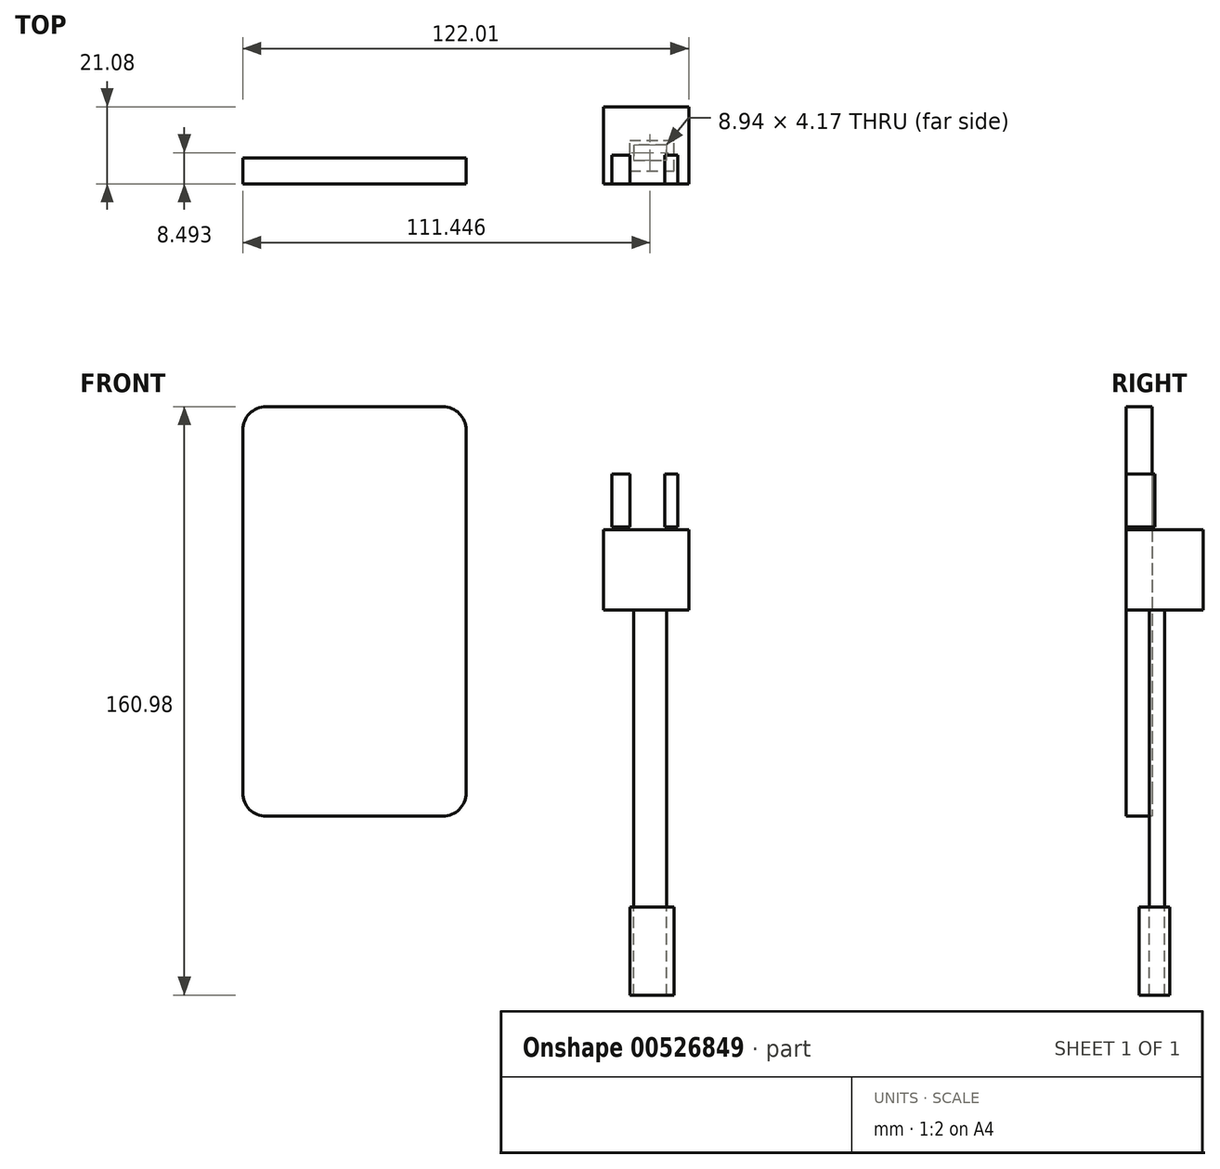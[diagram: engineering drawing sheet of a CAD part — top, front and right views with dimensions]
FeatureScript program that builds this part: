
annotation { "Feature Type Name" : "Feature", "Feature Type Description" : "" }
export const myFeature = defineFeature(function(context is Context, id is Id, definition is map)
    precondition{}
    {
        {
            var Q0;
            Q0=qCreatedBy(makeId("Front.planeOp"),FACE);
            var sketch = newSketch(context, id + "F0", { "sketchPlane" : qUnion([Q0])});
            skLineSegment(sketch, "E0", {"start": v(-53.04, 49.22) * mm, "end": v(-53.04, -50.12) * mm});
            skLineSegment(sketch, "E1", {"start": v(-46.7, 55.57) * mm, "end": v(1.7, 55.57) * mm});
            skLineSegment(sketch, "E2", {"start": v(8.05, 49.22) * mm, "end": v(8.05, -50.12) * mm});
            skLineSegment(sketch, "E3", {"start": v(-46.7, -56.47) * mm, "end": v(1.7, -56.47) * mm});
            skPoint(sketch, "E4.visualSharp", {"position": v(-53.04, 55.57) * mm});
            skArc(sketch, "E4.filletArc", {"start": v(-46.7, 55.57) * mm, "mid": v(-51.18, 53.72) * mm, "end": v(-53.04, 49.22) * mm});
            skPoint(sketch, "E5.visualSharp", {"position": v(8.05, 55.57) * mm});
            skArc(sketch, "E5.filletArc", {"start": v(8.05, 49.22) * mm, "mid": v(6.19, 53.72) * mm, "end": v(1.7, 55.57) * mm});
            skPoint(sketch, "E6.visualSharp", {"position": v(8.05, -56.47) * mm});
            skArc(sketch, "E6.filletArc", {"start": v(1.7, -56.47) * mm, "mid": v(6.19, -54.6) * mm, "end": v(8.05, -50.12) * mm});
            skPoint(sketch, "E7.visualSharp", {"position": v(-53.04, -56.47) * mm});
            skArc(sketch, "E7.filletArc", {"start": v(-53.04, -50.12) * mm, "mid": v(-51.18, -54.6) * mm, "end": v(-46.7, -56.47) * mm});
            skLineSegment(sketch, "E8", {"start": v(-43.71, 45.44) * mm, "end": v(-2.48, 45.44) * mm});
            skLineSegment(sketch, "E9", {"start": v(-50.06, 39.1) * mm, "end": v(-50.06, -39.99) * mm});
            skLineSegment(sketch, "E10", {"start": v(-43.71, -46.34) * mm, "end": v(-2.48, -46.34) * mm});
            skLineSegment(sketch, "E11", {"start": v(3.87, 39.1) * mm, "end": v(3.87, -39.99) * mm});
            skPoint(sketch, "E12.visualSharp", {"position": v(-50.06, 45.44) * mm});
            skArc(sketch, "E12.filletArc", {"start": v(-43.71, 45.44) * mm, "mid": v(-48.2, 43.58) * mm, "end": v(-50.06, 39.1) * mm});
            skPoint(sketch, "E13.visualSharp", {"position": v(3.87, 45.44) * mm});
            skArc(sketch, "E13.filletArc", {"start": v(3.87, 39.1) * mm, "mid": v(2.01, 43.58) * mm, "end": v(-2.48, 45.44) * mm});
            skPoint(sketch, "E14.visualSharp", {"position": v(3.87, -46.34) * mm});
            skArc(sketch, "E14.filletArc", {"start": v(-2.48, -46.34) * mm, "mid": v(2.01, -44.48) * mm, "end": v(3.87, -39.99) * mm});
            skPoint(sketch, "E15.visualSharp", {"position": v(-50.06, -46.34) * mm});
            skArc(sketch, "E15.filletArc", {"start": v(-50.06, -39.99) * mm, "mid": v(-48.2, -44.48) * mm, "end": v(-43.71, -46.34) * mm});
            skSolve(sketch);
        }
        {
            var Q0;
            Q0=makeQuery(id+"F0.imprint","IMPRINT",FACE,{"disambiguationData":[TD([[makeQuery(id+"F0.imprint","IMPRINT",EDGE,{"derivedFrom":sQuery(id+"F0.wireOp",EDGE,"E8")}),-1.0]])]});
            var Q1;
            Q1=makeQuery(id+"F0.imprint","IMPRINT",FACE,{"disambiguationData":[TD([[makeQuery(id+"F0.imprint","IMPRINT",EDGE,{"derivedFrom":sQuery(id+"F0.wireOp",EDGE,"E0")}),1.0]])]});
            extrude(context, id + "F1", {"entities" : qUnion([Q0, Q1]), "oppositeDirection" : true, "depth" : 7.11 * mm, "offsetDistance" : 25.4 * mm});
        }
        {
            var Q0;
            Q0=makeQuery(id+"F1.opExtrude","CAP_FACE",FACE,{"disambiguationData":[OSD([sQuery(id+"F0.wireOp",EDGE,"E0"),sQuery(id+"F0.wireOp",EDGE,"E1"),sQuery(id+"F0.wireOp",EDGE,"E2"),sQuery(id+"F0.wireOp",EDGE,"E3"),sQuery(id+"F0.wireOp",EDGE,"E4.filletArc"),sQuery(id+"F0.wireOp",EDGE,"E5.filletArc"),sQuery(id+"F0.wireOp",EDGE,"E6.filletArc"),sQuery(id+"F0.wireOp",EDGE,"E7.filletArc")])],"isStart":false});
            var sketch = newSketch(context, id + "F2", { "sketchPlane" : qUnion([Q0])});
            skLineSegment(sketch, "E16", {"start": v(-8.05, 44.55) * mm, "end": v(53.04, 44.55) * mm});
            skLineSegment(sketch, "E17", {"start": v(-8.05, -44.85) * mm, "end": v(53.04, -44.85) * mm});
            skCircle(sketch, "E18", {"center": v(-1.7, 49.22) * mm, "radius": 3.2 * mm});
            skSolve(sketch);
        }
        {
            var Q0;
            {var subQ0=sQuery(id+"F2.wireOp",EDGE,"E16");Q0=makeQuery(id+"F2.imprint","IMPRINT",FACE,{"disambiguationData":[TD([[makeQuery(id+"F2.imprint","IMPRINT",EDGE,{"derivedFrom":subQ0}),-1.0]])]});}
            var sketch = newSketch(context, id + "F3", { "sketchPlane" : qUnion([Q0])});
            skCircle(sketch, "E19", {"center": v(21.16, 26.37) * mm, "radius": 11.46 * mm});
            skSolve(sketch);
        }
        {
            var Q0;
            Q0=qCreatedBy(makeId("Front.planeOp"),FACE);
            var sketch = newSketch(context, id + "F4", { "sketchPlane" : qUnion([Q0])});
            skLineSegment(sketch, "E20.bottom", {"start": v(45.71, 21.97) * mm, "end": v(68.97, 21.97) * mm});
            skLineSegment(sketch, "E20.top", {"start": v(45.71, 0) * mm, "end": v(68.97, 0) * mm});
            skLineSegment(sketch, "E20.left", {"start": v(45.71, 21.97) * mm, "end": v(45.71, 0) * mm});
            skLineSegment(sketch, "E20.right", {"start": v(68.97, 21.97) * mm, "end": v(68.97, 0) * mm});
            skSolve(sketch);
        }
        {
            var Q0;
            Q0 = qSketchRegion(id + "F4", true);
            extrude(context, id + "F5", {"entities" : qUnion([Q0]), "oppositeDirection" : true, "depth" : 21.08 * mm, "offsetDistance" : 25.4 * mm});
        }
        {
            var Q0;
            Q0=makeQuery(id+"F5.opExtrude","SWEPT_FACE",FACE,{"disambiguationData":[OSD([sQuery(id+"F4.wireOp",EDGE,"E20.top")])]});
            var sketch = newSketch(context, id + "F6", { "sketchPlane" : qUnion([Q0])});
            skLineSegment(sketch, "E21.bottom", {"start": v(53.9, -6.42) * mm, "end": v(63.07, -6.42) * mm});
            skLineSegment(sketch, "E21.top", {"start": v(53.9, -10.59) * mm, "end": v(63.07, -10.59) * mm});
            skLineSegment(sketch, "E21.left", {"start": v(53.9, -6.42) * mm, "end": v(53.9, -10.59) * mm});
            skLineSegment(sketch, "E21.right", {"start": v(63.07, -6.42) * mm, "end": v(63.07, -10.59) * mm});
            skLineSegment(sketch, "E22", {"start": v(57.34, -6.42) * mm, "end": v(57.34, -10.59) * mm});
            skPoint(sketch, "E22.startSnap0", {"position": v(57.34, 0) * mm});
            skSolve(sketch);
        }
        {
            var Q0;
            Q0=qCreatedBy(makeId("Front.planeOp"),FACE);
            var sketch = newSketch(context, id + "F7", { "sketchPlane" : qUnion([Q0])});
            skLineSegment(sketch, "E23", {"start": v(47.96, 22.65) * mm, "end": v(65.92, 22.65) * mm});
            skLineSegment(sketch, "E24", {"start": v(47.96, 22.65) * mm, "end": v(47.96, 37.2) * mm});
            skLineSegment(sketch, "E25", {"start": v(47.96, 37.2) * mm, "end": v(52.92, 37.2) * mm});
            skLineSegment(sketch, "E26", {"start": v(52.92, 37.2) * mm, "end": v(52.92, 22.65) * mm});
            skLineSegment(sketch, "E27", {"start": v(62.4, 22.65) * mm, "end": v(62.4, 37.2) * mm});
            skLineSegment(sketch, "E28", {"start": v(62.4, 37.2) * mm, "end": v(65.92, 37.2) * mm});
            skLineSegment(sketch, "E29", {"start": v(65.92, 37.2) * mm, "end": v(65.92, 22.65) * mm});
            skSolve(sketch);
        }
        {
            var Q0;
            Q0 = qSketchRegion(id + "F7", true);
            extrude(context, id + "F8", {"entities" : qUnion([Q0]), "oppositeDirection" : true, "depth" : 7.87 * mm, "offsetDistance" : 25.4 * mm});
        }
        {
            var Q0;
            {var subQ4=sQuery(id+"F6.wireOp",EDGE,"E21.left");Q0=makeQuery(id+"F6.imprint","IMPRINT",FACE,{"disambiguationData":[TD([[makeQuery(id+"F6.imprint","IMPRINT",EDGE,{"derivedFrom":subQ4}),-1.0]])]});}
            var sketch = newSketch(context, id + "F9", { "sketchPlane" : qUnion([Q0])});
            skLineSegment(sketch, "E30", {"start": v(53.94, -6.4) * mm, "end": v(62.88, -6.4) * mm});
            skLineSegment(sketch, "E31", {"start": v(62.88, -6.4) * mm, "end": v(62.88, -10.58) * mm});
            skLineSegment(sketch, "E32", {"start": v(62.88, -10.58) * mm, "end": v(53.94, -10.58) * mm});
            skLineSegment(sketch, "E33", {"start": v(53.94, -10.58) * mm, "end": v(53.94, -6.4) * mm});
            skSolve(sketch);
        }
        {
            var Q0;
            Q0 = qSketchRegion(id + "F9", true);
            extrude(context, id + "F10", {"entities" : qUnion([Q0]), "operationType" : NewBodyOperationType.ADD, "depth" : 81.28 * mm, "offsetDistance" : 25.4 * mm});
        }
        {
            var Q0;
            Q0=makeQuery(id+"F10.opExtrude","CAP_FACE",FACE,{"disambiguationData":[OSD([sQuery(id+"F9.wireOp",EDGE,"E30"),sQuery(id+"F9.wireOp",EDGE,"E31"),sQuery(id+"F9.wireOp",EDGE,"E32"),sQuery(id+"F9.wireOp",EDGE,"E33")])],"isStart":false});
            var sketch = newSketch(context, id + "F11", { "sketchPlane" : qUnion([Q0])});
            skSolve(sketch);
        }
        {
            var Q0;
            Q0=makeQuery(id+"F11.imprint","IMPRINT",FACE,{"disambiguationData":[TD([[makeQuery(id+"F11.imprint","IMPRINT",EDGE,{"derivedFrom":makeQuery(id+"F10.opExtrude","CAP_EDGE",EDGE,{"disambiguationData":[OSD([sQuery(id+"F9.wireOp",EDGE,"E30")])],"isStart":false})}),-1.0]])]});
            var sketch = newSketch(context, id + "F12", { "sketchPlane" : qUnion([Q0])});
            skLineSegment(sketch, "E34.bottom", {"start": v(52.87, -3.58) * mm, "end": v(64.98, -3.58) * mm});
            skLineSegment(sketch, "E34.top", {"start": v(52.87, -11.94) * mm, "end": v(64.98, -11.94) * mm});
            skLineSegment(sketch, "E34.left", {"start": v(52.87, -3.58) * mm, "end": v(52.87, -11.94) * mm});
            skLineSegment(sketch, "E34.right", {"start": v(64.98, -3.58) * mm, "end": v(64.98, -11.94) * mm});
            skSolve(sketch);
        }
        {
            var Q0;
            Q0=makeQuery(id+"F12.imprint","IMPRINT",FACE,{"disambiguationData":[TD([[makeQuery(id+"F12.imprint","IMPRINT",EDGE,{"derivedFrom":sQuery(id+"F12.wireOp",EDGE,"E34.bottom")}),-1.0]])]});
            extrude(context, id + "F13", {"entities" : qUnion([Q0]), "depth" : 24.13 * mm, "offsetDistance" : 25.4 * mm});
        }
    });
